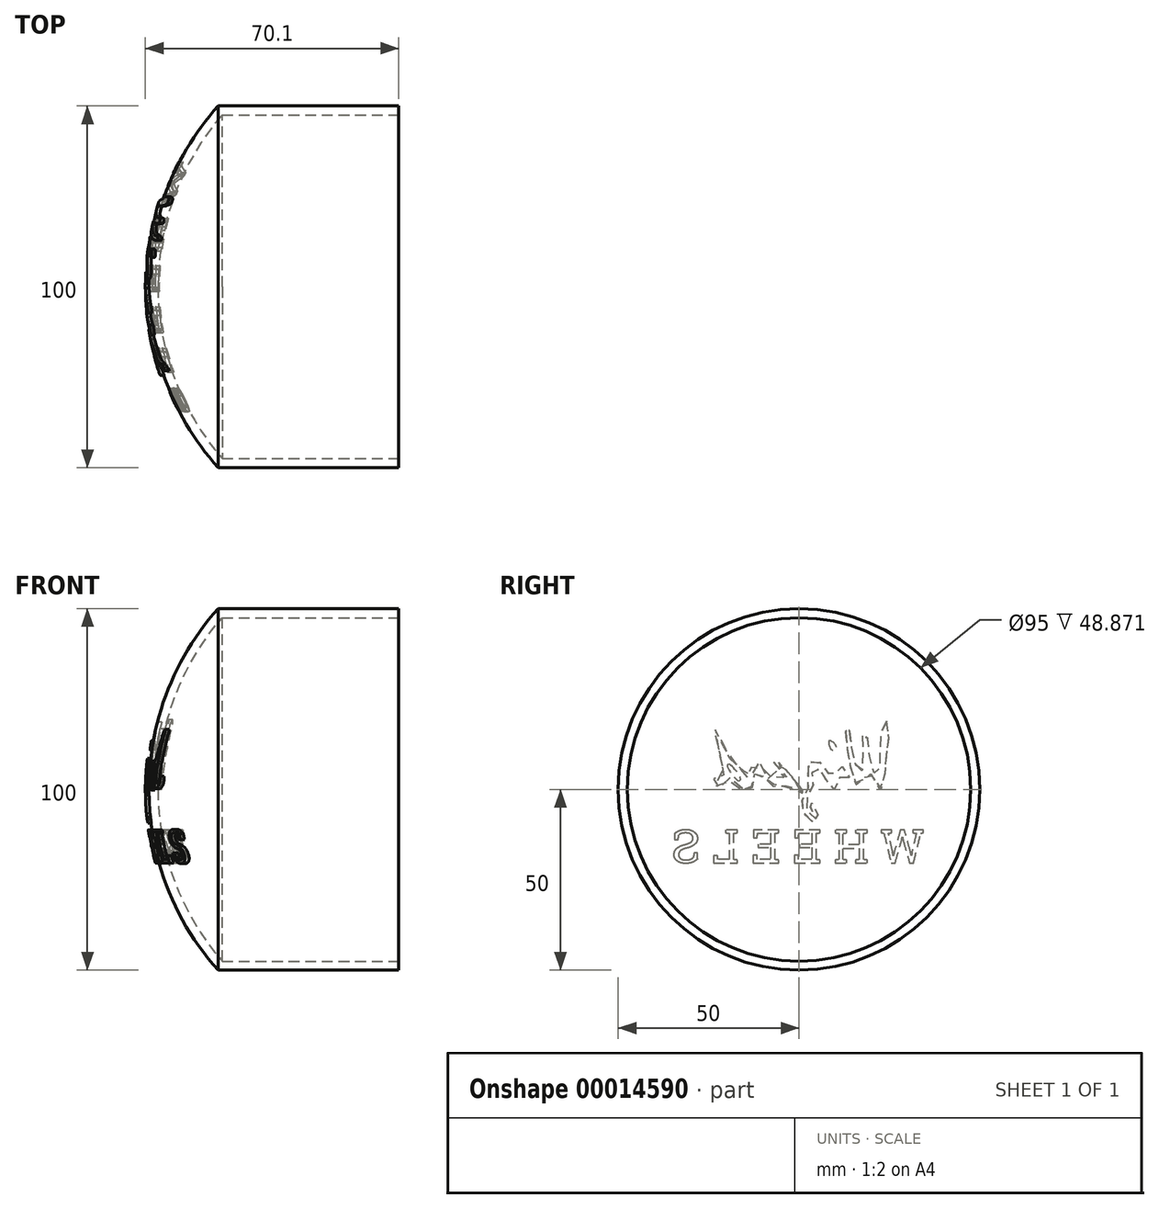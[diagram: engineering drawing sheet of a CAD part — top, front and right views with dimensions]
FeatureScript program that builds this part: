
annotation { "Feature Type Name" : "Feature", "Feature Type Description" : "" }
export const myFeature = defineFeature(function(context is Context, id is Id, definition is map)
    precondition{}
    {
        {
            var Q0;
            Q0=qCreatedBy(makeId("Front.planeOp"),FACE);
            var sketch = newSketch(context, id + "F0", { "sketchPlane" : qUnion([Q0])});
            skLineSegment(sketch, "E0", {"start": v(0, 50) * mm, "end": v(-50, 50) * mm});
            skLineSegment(sketch, "E1", {"start": v(0, 0) * mm, "end": v(0, 50) * mm});
            skArc(sketch, "E2", {"start": v(-50, 50) * mm, "mid": v(-64.16, 26.76) * mm, "end": v(-69.1, 0) * mm});
            skLineSegment(sketch, "E3", {"start": v(0, 0) * mm, "end": v(-96.64, 0) * mm, "construction": true});
            skLineSegment(sketch, "E4", {"start": v(-69.1, 0) * mm, "end": v(0, 0) * mm});
            skLineSegment(sketch, "E5", {"start": v(0, 0) * mm, "end": v(0, -46.86) * mm, "construction": true});
            skLineSegment(sketch, "E6", {"start": v(0, 0) * mm, "end": v(46.17, 0) * mm, "construction": true});
            skLineSegment(sketch, "E7", {"start": v(0, 0) * mm, "end": v(0, 59.8) * mm, "construction": true});
            skSolve(sketch);
        }
        {
            var Q0;
            Q0 = qSketchRegion(id + "F0", true);
            var Q1;
            Q1=sQuery(id+"F0.wireOp",EDGE,"E3");
            revolve(context, id + "F1", {"entities" : qUnion([Q0]), "axis" : qUnion([Q1]), "revolveType" : RevolveType.FULL});
        }
        {
            var Q0;
            Q0=makeQuery(id+"F1.opRevolve","SWEPT_FACE",FACE,{"disambiguationData":[OSD([sQuery(id+"F0.wireOp",EDGE,"E1")])]});
            shell(context, id + "F2", {"entities" : qUnion([Q0]), "thickness" : 2.5 * mm});
        }
        {
            var Q0;
            Q0=qCreatedBy(makeId("Front.planeOp"),FACE);
            var sketch = newSketch(context, id + "F3", { "sketchPlane" : qUnion([Q0])});
            skArc(sketch, "E8.0", {"start": v(-50.75, 50.67) * mm, "mid": v(-65.1, 27.12) * mm, "end": v(-70.1, 0) * mm});
            skSolve(sketch);
        }
        {
            var Q0;
            Q0 = qSketchRegion(id + "F3", true);
            var Q1;
            Q1=sQuery(id+"F3.wireOp",EDGE,"E8.0");
            var Q2;
            Q2=sQuery(id+"F0.wireOp",EDGE,"E3");
            revolve(context, id + "F4", {"bodyType" : ToolBodyType.SURFACE, "entities" : qUnion([Q0]), "surfaceEntities" : qUnion([Q1]), "axis" : qUnion([Q2]), "revolveType" : RevolveType.FULL});
        }
        {
            var Q0;
            Q0=sQuery(id+"F0.wireOp",EDGE,"E7");
            cPlane(context, id + "F5", {"entities" : qUnion([Q0]), "cplaneType" : CPlaneType.LINE_ANGLE, "offset" : 150 * mm, "angle" : 180 * degree, "width" : 150 * mm, "height" : 150 * mm});
        }
        {
            var Q0;
            Q0=qCreatedBy(id+"F5.planeOp",FACE);
            cPlane(context, id + "F6", {"entities" : qUnion([Q0]), "cplaneType" : CPlaneType.OFFSET, "offset" : 75 * mm, "width" : 150 * mm, "height" : 150 * mm});
        }
        {
            var Q0;
            Q0=sQuery(id+"F0.wireOp",EDGE,"E1");
            cPlane(context, id + "F7", {"entities" : qUnion([Q0]), "cplaneType" : CPlaneType.LINE_ANGLE, "offset" : 75 * mm, "angle" : 180 * degree, "width" : 150 * mm, "height" : 150 * mm});
        }
        {
            var Q0;
            Q0=qCreatedBy(id+"F7.planeOp",FACE);
            var sketch = newSketch(context, id + "F8", { "sketchPlane" : qUnion([Q0])});
            skText(sketch, "E9", { "text": "W H E E L S", "fontName": "RobotoSlab-Regular.ttf"});
            skLineSegment(sketch, "E10", {"start": v(0, 0) * mm, "end": v(0, 58.78) * mm, "construction": true});
            skLineSegment(sketch, "E11", {"start": v(0, 0) * mm, "end": v(-62.43, 0) * mm, "construction": true});
            skLineSegment(sketch, "E12", {"start": v(-35.9, -0.04) * mm, "end": v(34.3, -0.04) * mm, "construction": true});
            skFitSpline(sketch, "E13", {"points": [v(-24.29, 18.93) * mm, v(-24.65, 11.36) * mm, v(-24.34, 10.41) * mm, v(-22.58, -0.04) * mm, v(-18.85, 5.76) * mm, v(-17.8, 1.34) * mm, v(-16.06, 0.93) * mm, v(-13.07, 18.52) * mm, v(-13.64, 18.3) * mm, v(-14.15, 14.59) * mm, v(-16.84, 3.9) * mm, v(-17.63, 10.37) * mm, v(-17.8, 16.71) * mm, v(-18.69, 15.97) * mm, v(-19.34, 10.05) * mm, v(-21.89, 3) * mm, v(-23.13, 18.75) * mm, v(-24.29, 18.93) * mm]});
            skFitSpline(sketch, "E14", {"points": [v(-0.75, -0.88) * mm, v(1.03, 1.33) * mm, v(1.55, -0.06) * mm, v(6.4, 2.72) * mm, v(7.31, -0.04) * mm, v(8.5, 1.11) * mm, v(11.32, 5.89) * mm, v(12.26, 5.72) * mm, v(11.99, -0.06) * mm, v(14.54, 2.49) * mm, v(14.48, 1.03) * mm, v(16.2, -0.06) * mm, v(19.05, 3.27) * mm, v(19.36, 0.8) * mm, v(22.47, 0.61) * mm, v(24.08, 1.7) * mm, v(24.28, 2.12) * mm, v(24.39, 3.6) * mm, v(23.65, 2.84) * mm, v(21.24, 1.55) * mm, v(21.44, 7.36) * mm, v(23.15, 16.43) * mm, v(22.73, 16.43) * mm, v(20.02, 9.32) * mm, v(19.64, 8.9) * mm, v(16.3, 6.33) * mm, v(14.53, 3.69) * mm, v(13.02, 2.33) * mm, v(13.26, 6.29) * mm, v(11.62, 7.77) * mm, v(10.57, 7.55) * mm, v(10.5, 6.88) * mm, v(7.84, 2.2) * mm, v(7.23, 5.34) * mm, v(3.17, 2.24) * mm, v(3.17, 3.04) * mm, v(7.08, 7.57) * mm, v(6.94, 8.33) * mm, v(-1.05, -0.7) * mm, v(-0.75, -0.88) * mm]});
            skFitSpline(sketch, "E15", {"points": [v(19.34, 6.92) * mm, v(16.2, 2.95) * mm, v(16.8, 2.41) * mm, v(19.88, 6.63) * mm, v(19.34, 6.92) * mm]});
            skFitSpline(sketch, "E16", {"points": [v(-8.27, 13.38) * mm, v(-9.55, 12.91) * mm, v(-10.33, 11.14) * mm, v(-9.16, 10.86) * mm, v(-8.5, 11.68) * mm, v(-8.27, 13.38) * mm]});
            skFitSpline(sketch, "E17", {"points": [v(-13.97, 3.29) * mm, v(-11.23, 6.78) * mm, v(-10.52, 6.28) * mm, v(-9.43, 3.03) * mm, v(-7.95, 4.62) * mm, v(-4.3, 8.54) * mm, v(-2.82, 7.71) * mm, v(-2.45, 4.25) * mm, v(-3.07, 2.1) * mm, v(-1.7, -1.24) * mm, v(-0.83, -5.6) * mm, v(-3.81, -9.02) * mm, v(-5.1, -9.3) * mm, v(-5.5, -8.1) * mm, v(-2.89, -2.92) * mm, v(-2.4, -2.92) * mm, v(-4.71, -8.14) * mm, v(-1.86, -5.07) * mm, v(-4.03, 1.8) * mm, v(-3.53, 5.07) * mm, v(-4.9, 6.34) * mm, v(-9.67, -0.04) * mm, v(-11.68, 3.93) * mm, v(-13.6, 3.03) * mm, v(-13.97, 3.29) * mm]});
            const initialGuessF8  = {"E9": [-0.0346, -0.02035, 1, 0, 0.00928]};
            skSetInitialGuess(sketch, initialGuessF8);
            skSolve(sketch);
        }
        {
            var Q0;
            Q0 = qSketchRegion(id + "F8", true);
            var Q1;
            Q1=makeQuery(id+"F4.opRevolve","SWEPT_FACE",FACE,{"disambiguationData":[OSD([sQuery(id+"F3.wireOp",EDGE,"E8.0")])]});
            var Q2;
            Q2=makeQuery(id+"F2.opShell","OFFSET_FACE",FACE,{"disambiguationData":[OSD([sQuery(id+"F0.wireOp",EDGE,"E2")])]});
            extrude(context, id + "F9", {"entities" : qUnion([Q0]), "operationType" : NewBodyOperationType.ADD, "endBound" : BoundingType.UP_TO_SURFACE, "endBoundEntityFace" : qUnion([Q1]), "depth" : 25 * mm, "hasSecondDirection" : true, "secondDirectionBound" : SecondDirectionBoundingType.UP_TO_SURFACE, "secondDirectionOppositeDirection" : false, "secondDirectionBoundEntityFace" : qUnion([Q2]), "secondDirectionDepth" : 25 * mm});
        }
    });
